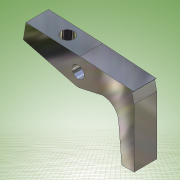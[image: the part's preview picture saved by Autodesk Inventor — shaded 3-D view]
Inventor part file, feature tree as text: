
AUTODESK INVENTOR PART (.ipt)
format: ipt  version: 2011 (Build 150239000, 239)  size: 165,888 bytes
history: native  units: in
note: dims shown in document units (in); Inventor stores cm internally (conversion verified against a paired STEP export)
features: extrude x5, sketch x5, fillet x1
ambient origin geometry x8: Origin, YZ Plane, XZ Plane, XY Plane, X Axis, Y Axis, Z Axis, Center Point
bodies: Solid1 (feature_tree)
feature tree (11):
  extrude  "Extrusion1"  Depth=0.573in
  extrude  "Extrusion2"  Depth=0.282in
  extrude  "Extrusion3"  Depth=0.219in
  extrude  "Extrusion4"  Depth=0.233in TaperAngle=0.0deg
  extrude  "Extrusion5"  Depth=0.14in TaperAngle=0.0deg
  fillet  "Fillet1"  Radius=0.025in
  sketch  "Sketch1"  dims[d4=0.126in d5=0.573in]
  sketch  "Sketch2"  dims[d6=0.085in d10=0.6358in d12=0.282in]
  sketch  "Sketch3"  dims[d14=0.0344in d17=0.219in]
  sketch  "Sketch4"  dims[d18=0.3208in d19=0.233in d20=0.0in]
  sketch  "Sketch5"  dims[d21=0.3125in d22=0.14in d23=0.0in d24=0.025in d28=0.14in d29=0.0in d30=0.14in d31=0.0in d32=0.14in d33=0.0in d34=0.002in]
